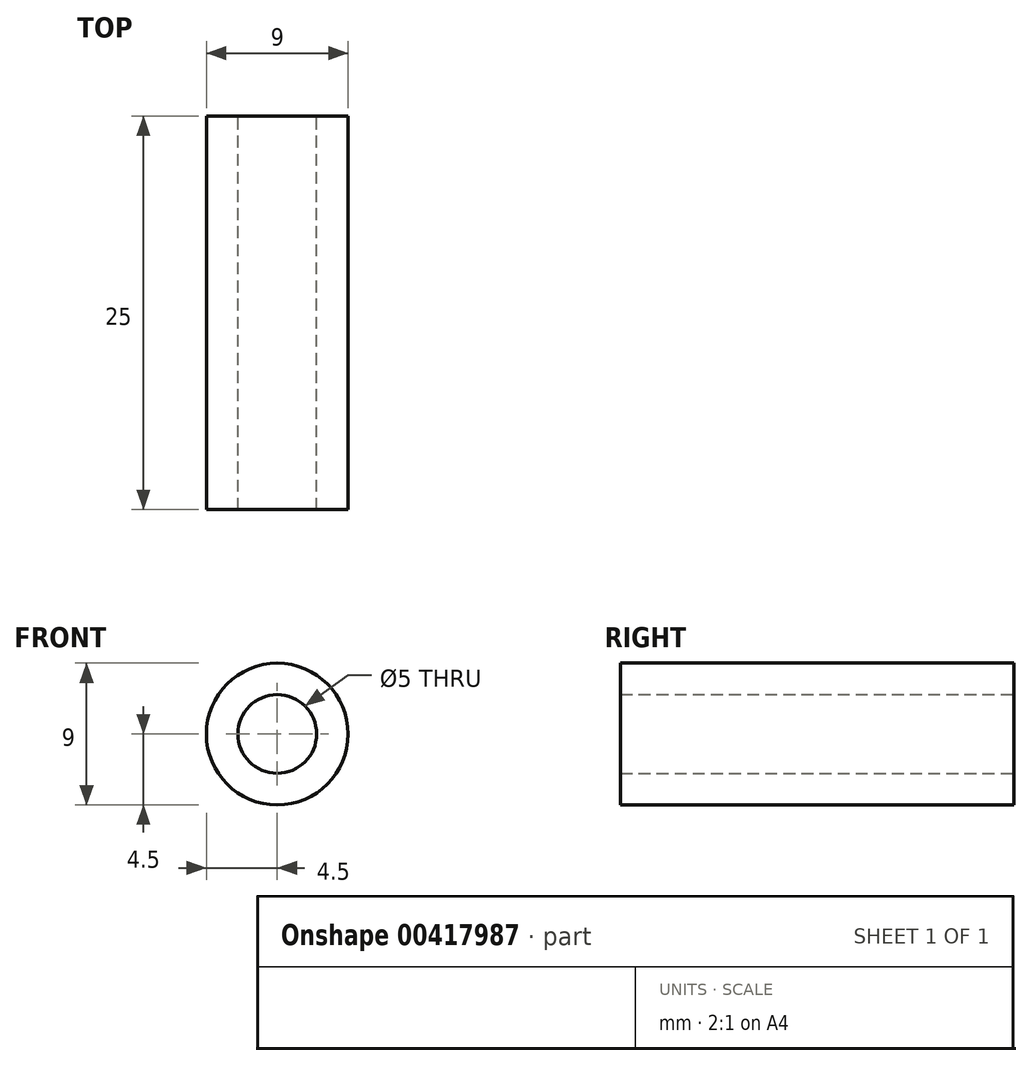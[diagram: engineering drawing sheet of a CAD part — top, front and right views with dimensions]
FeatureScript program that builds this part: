
annotation { "Feature Type Name" : "Feature", "Feature Type Description" : "" }
export const myFeature = defineFeature(function(context is Context, id is Id, definition is map)
    precondition{}
    {
        {
            var Q0;
            Q0=qCreatedBy(makeId("Front.planeOp"),FACE);
            var sketch = newSketch(context, id + "F0", { "sketchPlane" : qUnion([Q0])});
            skCircle(sketch, "E0", {"center": v(0, 0) * mm, "radius": 4.5 * mm});
            skCircle(sketch, "E1", {"center": v(0, 0) * mm, "radius": 2.5 * mm});
            skSolve(sketch);
        }
        {
            var Q0;
            Q0=makeQuery(id+"F0.imprint","IMPRINT",FACE,{"disambiguationData":[TD([[makeQuery(id+"F0.imprint","IMPRINT",EDGE,{"derivedFrom":sQuery(id+"F0.wireOp",EDGE,"E0")}),1.0]])]});
            extrude(context, id + "F1", {"entities" : qUnion([Q0]), "depth" : 25 * mm});
        }
    });
